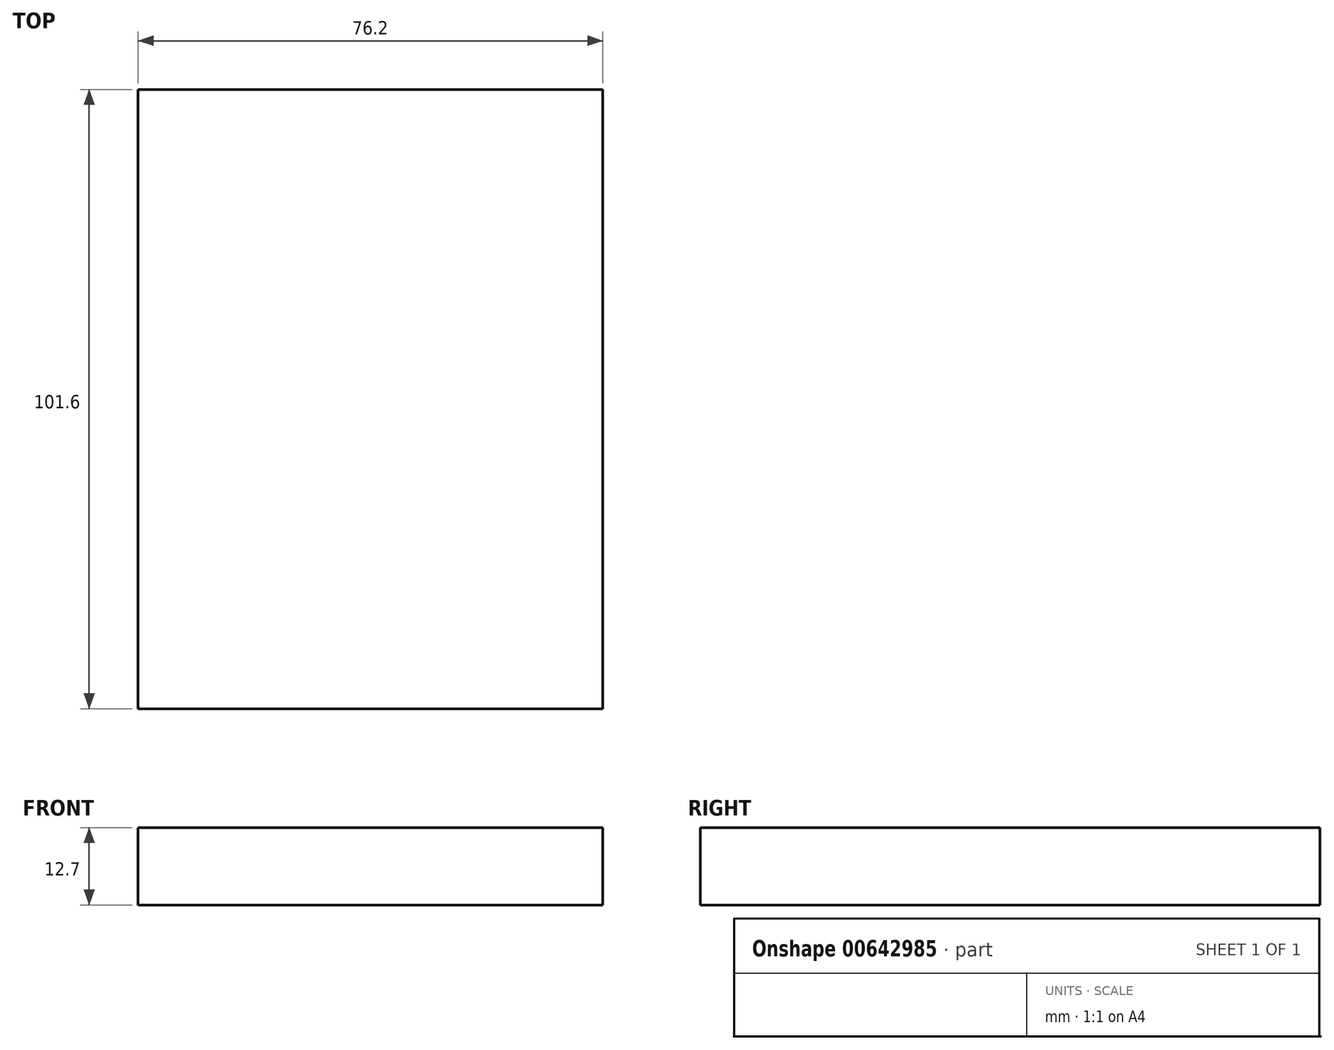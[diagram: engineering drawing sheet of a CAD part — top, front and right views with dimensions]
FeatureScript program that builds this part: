
annotation { "Feature Type Name" : "Feature", "Feature Type Description" : "" }
export const myFeature = defineFeature(function(context is Context, id is Id, definition is map)
    precondition{}
    {
        {
            var Q0;
            Q0=qCreatedBy(makeId("Top.planeOp"),FACE);
            var sketch = newSketch(context, id + "F0", { "sketchPlane" : qUnion([Q0])});
            skLineSegment(sketch, "E0.bottom", {"start": v(-33.78, 45.12) * mm, "end": v(42.42, 45.12) * mm});
            skLineSegment(sketch, "E0.top", {"start": v(-33.78, -56.48) * mm, "end": v(42.42, -56.48) * mm});
            skLineSegment(sketch, "E0.left", {"start": v(-33.78, 45.12) * mm, "end": v(-33.78, -56.48) * mm});
            skLineSegment(sketch, "E0.right", {"start": v(42.42, 45.12) * mm, "end": v(42.42, -56.48) * mm});
            skSolve(sketch);
        }
        {
            var Q0;
            Q0 = qSketchRegion(id + "F0", true);
            extrude(context, id + "F1", {"entities" : qUnion([Q0]), "depth" : 12.7 * mm, "offsetDistance" : 25.4 * mm});
        }
    });
